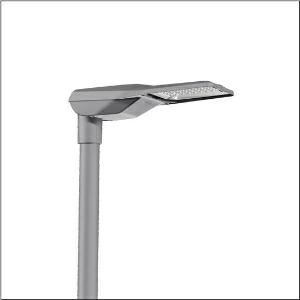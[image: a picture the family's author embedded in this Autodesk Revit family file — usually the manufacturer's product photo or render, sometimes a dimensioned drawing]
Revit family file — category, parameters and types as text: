
# Revit family: streetlight_sl_21_iq_mini___stw1_0a_5xe2e21g08hb_26c4
name_source: partatom
category: Lighting Fixtures
units: mm (PartAtom-declared; Revit-internal decimal feet)

## family parameters
Cut with Voids When Loaded = No
Host = Face
Light Source = No
Part Type = Normal
Room Calculation Point = No
Round Connector Dimension = Use Diameter
Shared = No

## types (1)
- --- (1 x LED, 7830 lm, 70.9 W, 2200K)
    Apparent Load = 71 VA
    CIE Flux Codes = 38 75 98 100 100
    Color Rendering = 70
    Color Temperature = 2200K
    Default Elevation = 1800 mm
    Description = Streetlight SL 21 iQ mini, mast luminaire, primary light control with lens, of PMMA, primary optical cover: cover, of toughened safety glass, transparent, light distribution: STW1.0a, light emission: direct distribution, primary light characteristic: asymmetric, installation type: post-top, side-entry, LED, High Power LED, rated luminous flux: 7.830lm, luminous efficacy: 110lm/W, light colour: 722, colour temperature: 2200K, control: Street-Remote, Auto-Match, Temp-Guard, Lumen-Switch, Night-Set, Smart-Wire, Light-Fading, Desk-Remote (wireless, voltage-free reading and setting of iQ features in the workshop via application-optimized NFC function/RFID function), optimised constant luminous flux control (CLO 2.0), presetting dimming linear, mains connection: 220..240V, AC, 50/60Hz, start of lifetime: 71W, end of service life: 75W, reduction: 31W, luminaire housing, of diecast aluminium, powder-coated, Siteco® metallic grey (DB 702S), corrosivity category C5 mid according to DIN EN ISO 12944, please order mast flange separately, inclination adjustable: 0°, 5°, 10°, 15°, sealing non-destructively replaceable, multi-level sealing system, length: 628mm, width: 235mm, height: 110mm, mast flange for spigot size: 42mm (side-entry): 5XC10008XM4, 60/48mm (side-entry/post-top): 5XC10108XM2, 76/60mm (side-entry/post-top): 5XC10108XM1, protection rating (complete): IP66, insulation class (complete): insulation class II (safety insulation), certification: CE, ENEC, ENEC+, VDE, impact resistance: IK09, permissible operating ambient temperature for outdoor applications: -40..+50°C, standard-compliant lighting for roads and squares, packaging unit: 1 piece

Light Distribution: STW1.0a
    Height = 110 mm
    Lamp = 1 x LED
    Lamp Light Flux = 7830 lm
    Lamp Power = 70.9 W
    Lamp count = 1
    Length = 625 mm
    Luminous efficacy = 110 lm/W
    Manufacturer = Siteco
    ModVariant = No
    Model = 5XE2E21G08HB
    Number of Poles = 1
    OnlyDefault = Yes
    Power Factor = 1
    Product Name = Streetlight SL 21 iQ mini | STW1.0a
    Product group = mast luminaire | pylon top
    ProductGroupID = 6100
    Protection Class = Protection class II
    Protection Degree = IP 66
    RLX_Detail_Level = 1
    RLX_Emergency_Light_Flux = 0 lm
    RLX_Emergency_Type = 0
    RLX_Emergency_Type_DB = No
    RlxData = <blob elided: 92297 chars, md5=99b921d0>
    Socket = socket
    Standby Power = 0 W
    System Light Flux = 7830 lm
    System Power = 71 W
    Type Comments = factory setting: luminous flux: 100 % | dim-lin: 254 | 711 mA
    Type Image = l_1003519.jpg
    URL = http://relux.com
    VarID = @adj_108157
    Voltage = 0 V
    Weight = 0.00 kg
    Width = 234 mm

## geometry (parser evidence)
native form markers: Blend x4, Sweep x10
no freeform markers — native parametric forms only
